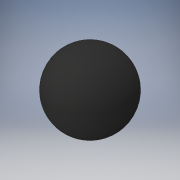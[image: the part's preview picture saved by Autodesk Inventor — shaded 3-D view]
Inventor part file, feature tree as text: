
AUTODESK INVENTOR PART (.ipt)
format: ipt  version: 2017 (Build 210142000, 142)  size: 120,320 bytes
history: native  units: in
note: dims shown in document units (in); Inventor stores cm internally (conversion verified against a paired STEP export)
features: fillet x2, sketch x2, extrude x1
ambient origin geometry x8: Origin, YZ Plane, XZ Plane, XY Plane, X Axis, Y Axis, Z Axis, Center Point
bodies: Solid1 (feature_tree)
feature tree (5):
  extrude  "Extrusion1"  Depth=10.5in TaperAngle=0.0deg
  fillet  "Fillet1"  Radius=10.5in
  sketch  "Sketch2"
  fillet  "Fillet2"  Radius=10.5in
  sketch  "Sketch1"  dims[d0=21.0in d1=21.0in d2=0.0in d3=10.5in d4=10.5in]
